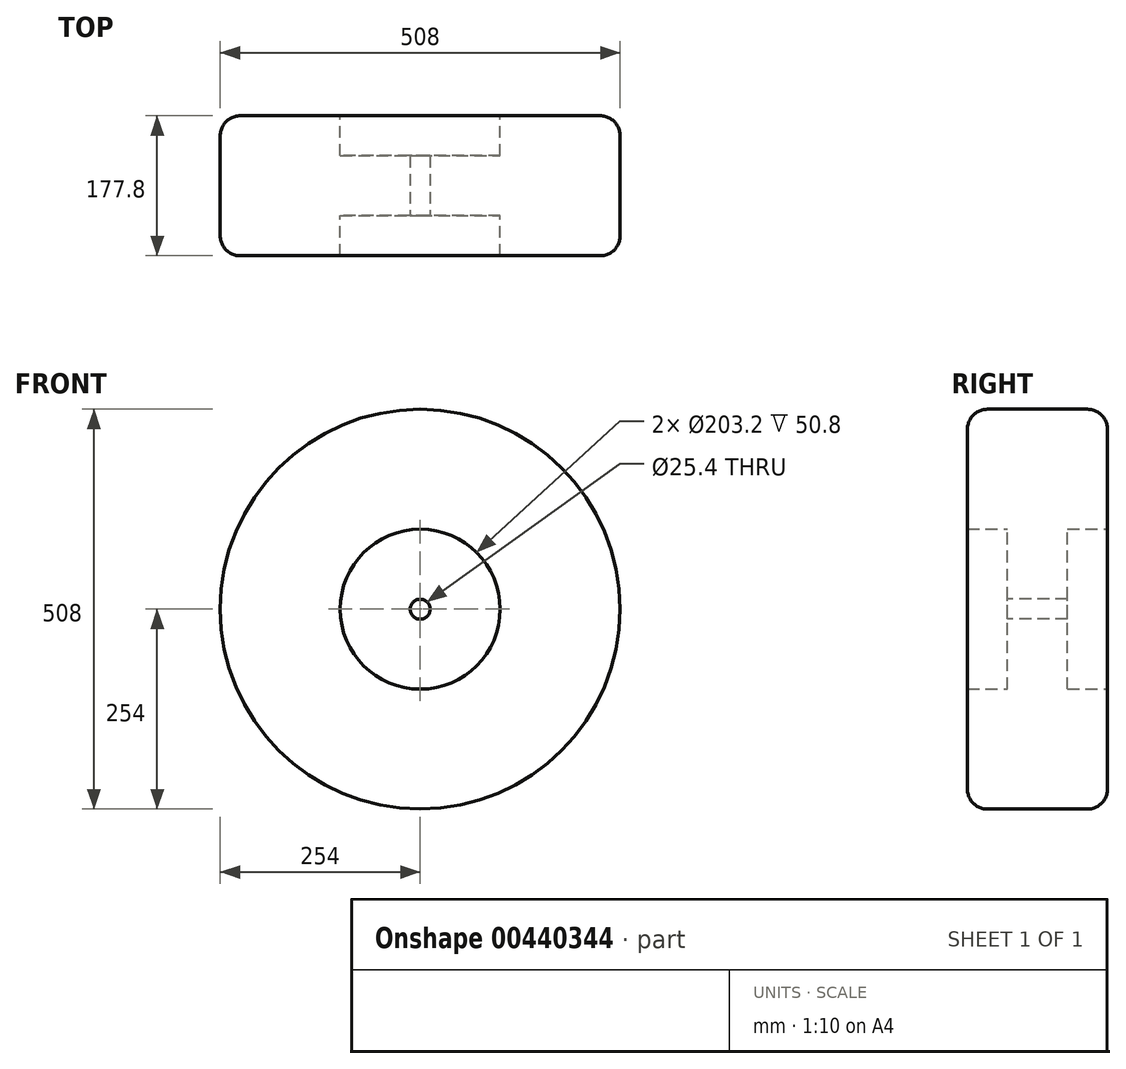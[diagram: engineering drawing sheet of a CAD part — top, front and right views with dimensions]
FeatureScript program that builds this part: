
annotation { "Feature Type Name" : "Feature", "Feature Type Description" : "" }
export const myFeature = defineFeature(function(context is Context, id is Id, definition is map)
    precondition{}
    {
        {
            var Q0;
            Q0=qCreatedBy(makeId("Front.planeOp"),FACE);
            var sketch = newSketch(context, id + "F0", { "sketchPlane" : qUnion([Q0])});
            skCircle(sketch, "E0", {"center": v(0, 0) * mm, "radius": 254 * mm});
            skSolve(sketch);
        }
        {
            var Q0;
            Q0=makeQuery(id+"F0.imprint","IMPRINT",FACE,{"disambiguationData":[TD([[makeQuery(id+"F0.imprint","IMPRINT",EDGE,{"derivedFrom":sQuery(id+"F0.wireOp",EDGE,"E0")}),1.0]])]});
            extrude(context, id + "F1", {"entities" : qUnion([Q0]), "endBound" : BoundingType.SYMMETRIC, "depth" : 177.8 * mm});
        }
        {
            var Q0;
            Q0=makeQuery(id+"F1.opExtrude","CAP_FACE",FACE,{"disambiguationData":[OSD([sQuery(id+"F0.wireOp",EDGE,"E0")])],"isStart":false});
            var sketch = newSketch(context, id + "F2", { "sketchPlane" : qUnion([Q0])});
            skCircle(sketch, "E1", {"center": v(0, 0) * mm, "radius": 101.6 * mm});
            skSolve(sketch);
        }
        {
            var Q0;
            Q0=makeQuery(id+"F2.imprint","IMPRINT",FACE,{"disambiguationData":[TD([[makeQuery(id+"F2.imprint","IMPRINT",EDGE,{"derivedFrom":sQuery(id+"F2.wireOp",EDGE,"E1")}),1.0]])]});
            extrude(context, id + "F3", {"entities" : qUnion([Q0]), "operationType" : NewBodyOperationType.REMOVE, "endBound" : BoundingType.SYMMETRIC, "depth" : 127 * mm});
        }
        {
            var Q0;
            Q0=makeQuery(id+"F1.opExtrude","CAP_FACE",FACE,{"disambiguationData":[OSD([sQuery(id+"F0.wireOp",EDGE,"E0")])],"isStart":false});
            var sketch = newSketch(context, id + "F4", { "sketchPlane" : qUnion([Q0])});
            skSolve(sketch);
        }
        {
            var Q0;
            Q0=makeQuery(id+"F4.imprint","IMPRINT",FACE,{"disambiguationData":[TD([[makeQuery(id+"F4.imprint","IMPRINT",EDGE,{"derivedFrom":makeQuery(id+"F3.boolean.opBoolean","INTERSECT",EDGE,{"derivedFrom":[makeQuery(id+"F1.opExtrude","CAP_FACE",FACE,{"disambiguationData":[OSD([sQuery(id+"F0.wireOp",EDGE,"E0")])],"isStart":false}),makeQuery(id+"F3.opExtrude","SWEPT_FACE",FACE,{"disambiguationData":[OSD([sQuery(id+"F2.wireOp",EDGE,"E1")])]})]})}),-1.0]])]});
            extrude(context, id + "F5", {"entities" : qUnion([Q0]), "operationType" : NewBodyOperationType.REMOVE, "endBound" : BoundingType.SYMMETRIC, "depth" : 355.6 * mm});
        }
        {
            var Q0;
            Q0=makeQuery(id+"F1.opExtrude","CAP_FACE",FACE,{"disambiguationData":[OSD([sQuery(id+"F0.wireOp",EDGE,"E0")])],"isStart":false});
            var sketch = newSketch(context, id + "F6", { "sketchPlane" : qUnion([Q0])});
            skCircle(sketch, "E2", {"center": v(0, 0) * mm, "radius": 101.6 * mm});
            skSolve(sketch);
        }
        {
            var Q0;
            Q0=makeQuery(id+"F6.imprint","IMPRINT",FACE,{"disambiguationData":[TD([[makeQuery(id+"F6.imprint","IMPRINT",EDGE,{"derivedFrom":sQuery(id+"F6.wireOp",EDGE,"E2")}),-1.0]])]});
            extrude(context, id + "F7", {"entities" : qUnion([Q0]), "operationType" : NewBodyOperationType.ADD, "endBound" : BoundingType.SYMMETRIC, "depth" : 127 * mm});
        }
        {
            var Q0;
            Q0=makeQuery(id+"F7.opExtrude","CAP_FACE",FACE,{"disambiguationData":[OSD([sQuery(id+"F6.wireOp",EDGE,"E2")])],"isStart":false});
            var sketch = newSketch(context, id + "F8", { "sketchPlane" : qUnion([Q0])});
            skCircle(sketch, "E3", {"center": v(0, 0) * mm, "radius": 101.6 * mm});
            skSolve(sketch);
        }
        {
            var Q0;
            Q0 = qSketchRegion(id + "F8", true);
            extrude(context, id + "F9", {"entities" : qUnion([Q0]), "operationType" : NewBodyOperationType.REMOVE, "endBound" : BoundingType.SYMMETRIC, "depth" : 355.6 * mm});
        }
        {
            var Q0;
            Q0=qCreatedBy(makeId("Front.planeOp"),FACE);
            var sketch = newSketch(context, id + "F10", { "sketchPlane" : qUnion([Q0])});
            skCircle(sketch, "E4", {"center": v(0, 0) * mm, "radius": 101.6 * mm});
            skSolve(sketch);
        }
        {
            var Q0;
            Q0=makeQuery(id+"F10.imprint","IMPRINT",FACE,{"disambiguationData":[TD([[makeQuery(id+"F10.imprint","IMPRINT",EDGE,{"derivedFrom":sQuery(id+"F10.wireOp",EDGE,"E4")}),1.0]])]});
            extrude(context, id + "F11", {"entities" : qUnion([Q0]), "operationType" : NewBodyOperationType.ADD, "endBound" : BoundingType.SYMMETRIC, "depth" : 76.2 * mm});
        }
        {
            var Q0;
            Q0=makeQuery(id+"F1.opExtrude","CAP_EDGE",EDGE,{"disambiguationData":[OSD([sQuery(id+"F0.wireOp",EDGE,"E0")])],"isStart":true});
            var Q1;
            Q1=makeQuery(id+"F1.opExtrude","CAP_EDGE",EDGE,{"disambiguationData":[OSD([sQuery(id+"F0.wireOp",EDGE,"E0")])],"isStart":false});
            fillet(context, id + "F12", {"entities" : qUnion([Q0, Q1]), "radius" : 25.4 * mm, "tangentPropagation" : true, "allowEdgeOverflow" : false});
        }
        {
            var Q0;
            Q0=makeQuery(id+"F11.opExtrude","CAP_FACE",FACE,{"disambiguationData":[OSD([sQuery(id+"F10.wireOp",EDGE,"E4")])],"isStart":true});
            var sketch = newSketch(context, id + "F13", { "sketchPlane" : qUnion([Q0])});
            skCircle(sketch, "E5", {"center": v(0, 0) * mm, "radius": 12.7 * mm});
            skSolve(sketch);
        }
        {
            var Q0;
            Q0=makeQuery(id+"F13.imprint","IMPRINT",FACE,{"disambiguationData":[TD([[makeQuery(id+"F13.imprint","IMPRINT",EDGE,{"derivedFrom":sQuery(id+"F13.wireOp",EDGE,"E5")}),1.0]])]});
            extrude(context, id + "F14", {"entities" : qUnion([Q0]), "operationType" : NewBodyOperationType.REMOVE, "endBound" : BoundingType.SYMMETRIC, "depth" : 355.6 * mm});
        }
    });
